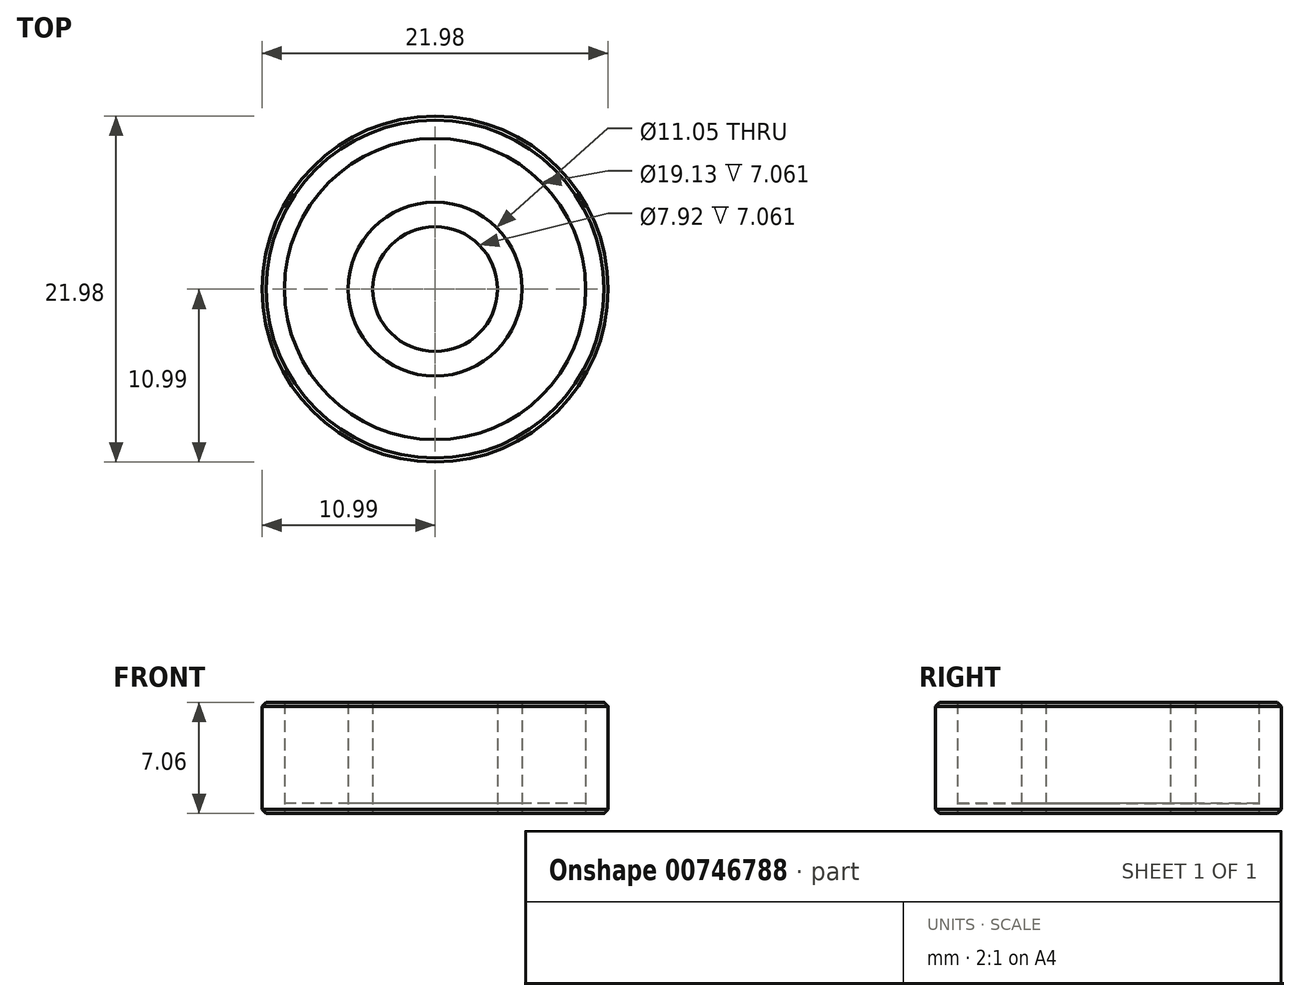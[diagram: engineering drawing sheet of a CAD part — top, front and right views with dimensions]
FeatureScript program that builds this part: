
annotation { "Feature Type Name" : "Feature", "Feature Type Description" : "" }
export const myFeature = defineFeature(function(context is Context, id is Id, definition is map)
    precondition{}
    {
        {
            var Q0;
            Q0=qCreatedBy(makeId("Top.planeOp"),FACE);
            var sketch = newSketch(context, id + "F0", { "sketchPlane" : qUnion([Q0])});
            skCircle(sketch, "E0", {"center": v(0, 0) * mm, "radius": 10.99 * mm});
            skCircle(sketch, "E1", {"center": v(0, 0) * mm, "radius": 9.56 * mm});
            skCircle(sketch, "E2", {"center": v(0, 0) * mm, "radius": 5.52 * mm});
            skCircle(sketch, "E3", {"center": v(0, 0) * mm, "radius": 3.96 * mm});
            skSolve(sketch);
        }
        {
            var Q0;
            Q0=makeQuery(id+"F0.imprint","IMPRINT",FACE,{"disambiguationData":[TD([[makeQuery(id+"F0.imprint","IMPRINT",EDGE,{"derivedFrom":sQuery(id+"F0.wireOp",EDGE,"E0")}),1.0]])]});
            var Q1;
            Q1=makeQuery(id+"F0.imprint","IMPRINT",FACE,{"disambiguationData":[TD([[makeQuery(id+"F0.imprint","IMPRINT",EDGE,{"derivedFrom":sQuery(id+"F0.wireOp",EDGE,"E2")}),1.0]])]});
            extrude(context, id + "F1", {"entities" : qUnion([Q0, Q1]), "depth" : 7.06 * mm, "offsetDistance" : 25.4 * mm});
        }
        {
            var Q0;
            Q0=makeQuery(id+"F1.opExtrude","CAP_FACE",FACE,{"disambiguationData":[OSD([sQuery(id+"F0.wireOp",EDGE,"E0")])],"isStart":false});
            var Q1;
            Q1=makeQuery(id+"F1.opExtrude","CAP_FACE",FACE,{"disambiguationData":[OSD([sQuery(id+"F0.wireOp",EDGE,"E0")])],"isStart":true});
            cPlane(context, id + "F2", {"entities" : qUnion([Q0, Q1]), "cplaneType" : CPlaneType.MID_PLANE, "offset" : 25.4 * mm, "width" : 152.4 * mm, "height" : 152.4 * mm});
        }
        {
            var Q0;
            Q0=makeQuery(id+"F0.imprint","IMPRINT",FACE,{"disambiguationData":[TD([[makeQuery(id+"F0.imprint","IMPRINT",EDGE,{"derivedFrom":sQuery(id+"F0.wireOp",EDGE,"E1")}),1.0]])]});
            var Q1;
            Q1=makeQuery(id+"F1.opExtrude","CAP_FACE",FACE,{"disambiguationData":[OSD([sQuery(id+"F0.wireOp",EDGE,"E0"),sQuery(id+"F0.wireOp",EDGE,"E1")])],"isStart":false});
            extrude(context, id + "F3", {"entities" : qUnion([Q0]), "endBound" : BoundingType.UP_TO_SURFACE, "depth" : 25.4 * mm, "endBoundEntityFace" : qUnion([Q1]), "offsetDistance" : 25.4 * mm});
        }
        {
            var Q0;
            Q0=makeQuery(id+"F0.imprint","IMPRINT",FACE,{"disambiguationData":[TD([[makeQuery(id+"F0.imprint","IMPRINT",EDGE,{"derivedFrom":sQuery(id+"F0.wireOp",EDGE,"E1")}),1.0]])]});
            extrude(context, id + "F4", {"entities" : qUnion([Q0]), "operationType" : NewBodyOperationType.REMOVE, "depth" : 0.64 * mm, "offsetDistance" : 25.4 * mm});
        }
        {
            var Q0;
            Q0=makeQuery(id+"F0.imprint","IMPRINT",FACE,{"disambiguationData":[TD([[makeQuery(id+"F0.imprint","IMPRINT",EDGE,{"derivedFrom":sQuery(id+"F0.wireOp",EDGE,"E3")}),1.0]])]});
            extrude(context, id + "F5", {"entities" : qUnion([Q0]), "operationType" : NewBodyOperationType.REMOVE, "depth" : 25.4 * mm, "offsetDistance" : 25.4 * mm});
        }
        {
            var Q0;
            Q0=makeQuery(id+"F1.opExtrude","SWEPT_FACE",FACE,{"disambiguationData":[OSD([sQuery(id+"F0.wireOp",EDGE,"E0")])]});
            chamfer(context, id + "F6", {"entities" : qUnion([Q0]), "width" : 0.25 * mm, "tangentPropagation" : true});
        }
    });
